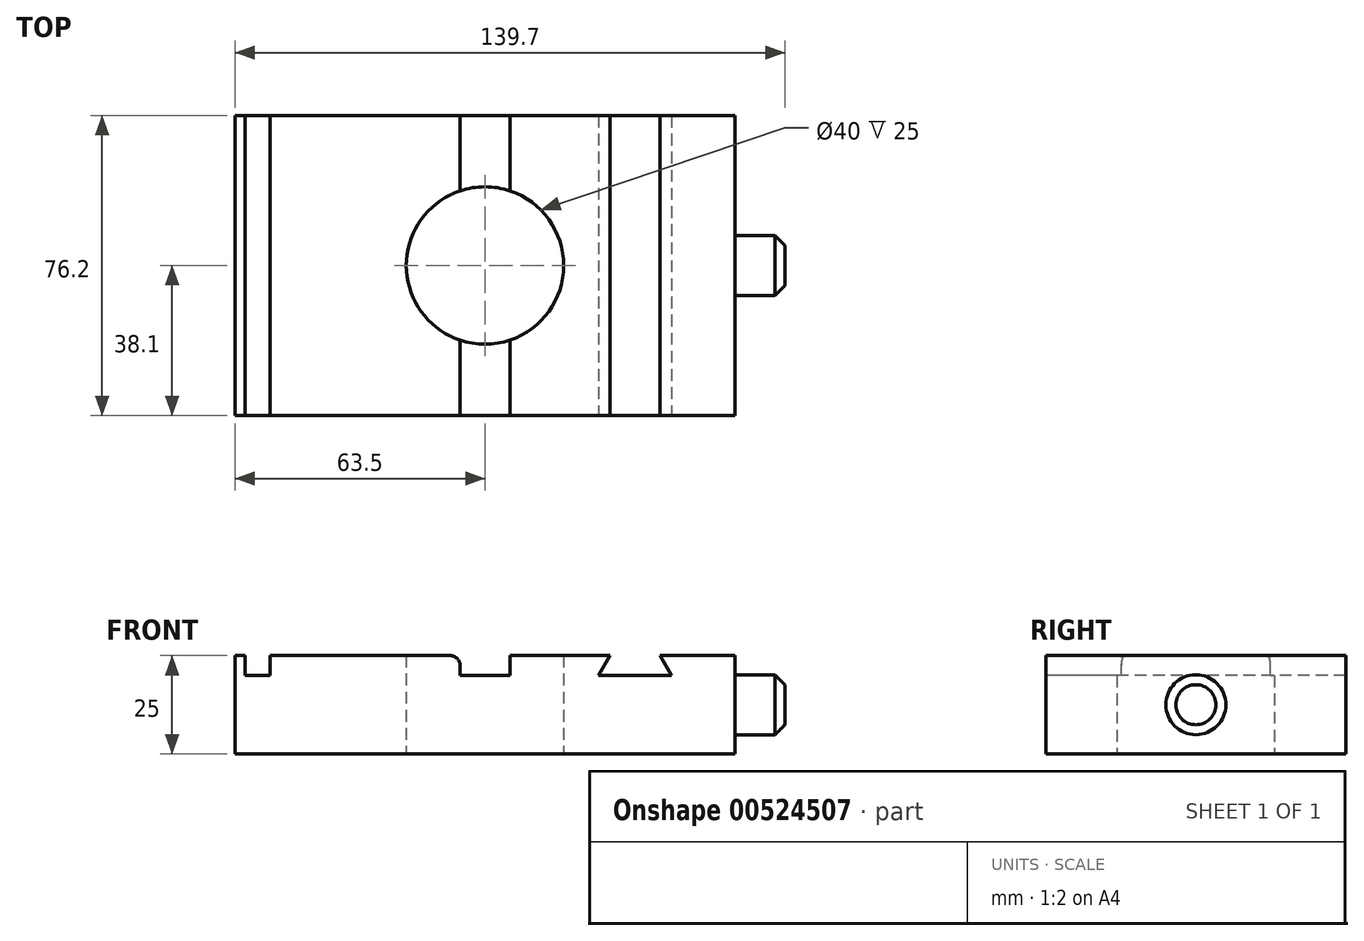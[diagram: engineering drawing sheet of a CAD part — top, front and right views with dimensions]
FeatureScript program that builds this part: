
annotation { "Feature Type Name" : "Feature", "Feature Type Description" : "" }
export const myFeature = defineFeature(function(context is Context, id is Id, definition is map)
    precondition{}
    {
        {
            var Q0;
            Q0=qCreatedBy(makeId("Top.planeOp"),FACE);
            var sketch = newSketch(context, id + "F0", { "sketchPlane" : qUnion([Q0])});
            skLineSegment(sketch, "E0.bottom", {"start": v(63.5, -38.1) * mm, "end": v(-63.5, -38.1) * mm});
            skLineSegment(sketch, "E0.top", {"start": v(63.5, 38.1) * mm, "end": v(-63.5, 38.1) * mm});
            skLineSegment(sketch, "E0.left", {"start": v(63.5, -38.1) * mm, "end": v(63.5, 38.1) * mm});
            skLineSegment(sketch, "E0.right", {"start": v(-63.5, -38.1) * mm, "end": v(-63.5, 38.1) * mm});
            skPoint(sketch, "E0.middle", {"position": v(0, 0) * mm});
            skCircle(sketch, "E1", {"center": v(0, 0) * mm, "radius": 20 * mm});
            skSolve(sketch);
        }
        {
            var Q0;
            Q0=makeQuery(id+"F0.imprint","IMPRINT",FACE,{"disambiguationData":[TD([[makeQuery(id+"F0.imprint","IMPRINT",EDGE,{"derivedFrom":sQuery(id+"F0.wireOp",EDGE,"E0.bottom")}),-1.0]])]});
            extrude(context, id + "F1", {"entities" : qUnion([Q0]), "depth" : 25 * mm, "offsetDistance" : 25 * mm});
        }
        {
            var Q0;
            Q0=makeQuery(id+"F1.opExtrude","CAP_FACE",FACE,{"disambiguationData":[OSD([sQuery(id+"F0.wireOp",EDGE,"E0.bottom"),sQuery(id+"F0.wireOp",EDGE,"E0.top"),sQuery(id+"F0.wireOp",EDGE,"E0.left"),sQuery(id+"F0.wireOp",EDGE,"E0.right"),sQuery(id+"F0.wireOp",EDGE,"E1")])],"isStart":false});
            var sketch = newSketch(context, id + "F2", { "sketchPlane" : qUnion([Q0])});
            skLineSegment(sketch, "E2.bottom", {"start": v(-60.96, 38.1) * mm, "end": v(-54.6, 38.1) * mm});
            skLineSegment(sketch, "E2.top", {"start": v(-60.96, -38.1) * mm, "end": v(-54.6, -38.1) * mm});
            skLineSegment(sketch, "E2.left", {"start": v(-60.96, 38.1) * mm, "end": v(-60.96, -38.1) * mm});
            skLineSegment(sketch, "E2.right", {"start": v(-54.6, 38.1) * mm, "end": v(-54.6, -38.1) * mm});
            skLineSegment(sketch, "E3", {"start": v(-6.35, 38.1) * mm, "end": v(-6.35, -38.1) * mm});
            skLineSegment(sketch, "E4", {"start": v(-6.35, -38.1) * mm, "end": v(6.35, -38.1) * mm});
            skLineSegment(sketch, "E5", {"start": v(6.35, -38.1) * mm, "end": v(6.35, 38.1) * mm});
            skPoint(sketch, "E6", {"position": v(0, 0) * mm});
            skLineSegment(sketch, "E7", {"start": v(-6.35, 38.1) * mm, "end": v(6.35, 38.1) * mm, "construction": true});
            skLineSegment(sketch, "E8", {"start": v(0, 38.1) * mm, "end": v(0, -38.1) * mm, "construction": true});
            skSolve(sketch);
        }
        {
            var Q0;
            Q0=makeQuery(id+"F2.imprint","IMPRINT",FACE,{"disambiguationData":[TD([[makeQuery(id+"F2.imprint","IMPRINT",EDGE,{"derivedFrom":sQuery(id+"F2.wireOp",EDGE,"E2.bottom")}),1.0]])]});
            var Q1;
            {var subQ0=sQuery(id+"F2.wireOp",EDGE,"E4");Q1=makeQuery(id+"F2.imprint","IMPRINT",FACE,{"disambiguationData":[TD([[makeQuery(id+"F2.imprint","IMPRINT",EDGE,{"derivedFrom":subQ0}),-1.0]])]});}
            var Q2;
            {var subQ0=sQuery(id+"F2.wireOp",EDGE,"E3");var subQ1=makeQuery(id+"F1.opExtrude","CAP_EDGE",EDGE,{"disambiguationData":[OSD([sQuery(id+"F0.wireOp",EDGE,"E0.top")])],"isStart":false});var subQ2=makeQuery(id+"F2.imprint","INTERSECT",VERTEX,{"derivedFrom":[subQ1,subQ0]});Q2=makeQuery(id+"F2.imprint","IMPRINT",FACE,{"disambiguationData":[TD([[makeQuery(id+"F2.imprint","IMPRINT",EDGE,{"disambiguationData":[TD([[subQ2,-1.0]])],"derivedFrom":subQ0}),1.0]])]});}
            extrude(context, id + "F3", {"entities" : qUnion([Q0, Q1, Q2]), "operationType" : NewBodyOperationType.REMOVE, "oppositeDirection" : true, "depth" : 5.08 * mm, "offsetDistance" : 25.4 * mm});
        }
        {
            var Q0;
            Q0=makeQuery(id+"F1.opExtrude","SWEPT_FACE",FACE,{"disambiguationData":[OSD([sQuery(id+"F0.wireOp",EDGE,"E0.bottom")])]});
            var sketch = newSketch(context, id + "F4", { "sketchPlane" : qUnion([Q0])});
            skLineSegment(sketch, "E9", {"start": v(31.75, 25) * mm, "end": v(28.82, 19.92) * mm});
            skLineSegment(sketch, "E10", {"start": v(28.82, 19.92) * mm, "end": v(47.38, 19.92) * mm});
            skLineSegment(sketch, "E11", {"start": v(47.38, 19.92) * mm, "end": v(44.45, 25) * mm});
            skLineSegment(sketch, "E12", {"start": v(44.45, 25) * mm, "end": v(31.75, 25) * mm});
            skLineSegment(sketch, "E13", {"start": v(38.1, 19.92) * mm, "end": v(38.1, 25) * mm, "construction": true});
            skSolve(sketch);
        }
        {
            var Q0;
            Q0=makeQuery(id+"F4.imprint","IMPRINT",FACE,{"disambiguationData":[TD([[makeQuery(id+"F4.imprint","IMPRINT",EDGE,{"derivedFrom":sQuery(id+"F4.wireOp",EDGE,"E9")}),1.0]])]});
            extrude(context, id + "F5", {"entities" : qUnion([Q0]), "operationType" : NewBodyOperationType.REMOVE, "endBound" : BoundingType.THROUGH_ALL, "oppositeDirection" : true, "depth" : 25.4 * mm, "offsetDistance" : 25.4 * mm});
        }
        {
            var Q0;
            Q0=makeQuery(id+"F1.opExtrude","SWEPT_FACE",FACE,{"disambiguationData":[OSD([sQuery(id+"F0.wireOp",EDGE,"E0.left")])]});
            var sketch = newSketch(context, id + "F6", { "sketchPlane" : qUnion([Q0])});
            skCircle(sketch, "E14", {"center": v(0, 12.5) * mm, "radius": 7.62 * mm});
            skPoint(sketch, "E14.centerSnap0", {"position": v(0, 25) * mm});
            skPoint(sketch, "E14.centerSnap1", {"position": v(-38.1, 12.5) * mm});
            skSolve(sketch);
        }
        {
            var Q0;
            Q0=makeQuery(id+"F6.imprint","IMPRINT",FACE,{"disambiguationData":[TD([[makeQuery(id+"F6.imprint","IMPRINT",EDGE,{"derivedFrom":sQuery(id+"F6.wireOp",EDGE,"E14")}),1.0]])]});
            extrude(context, id + "F7", {"entities" : qUnion([Q0]), "operationType" : NewBodyOperationType.ADD, "depth" : 12.7 * mm, "offsetDistance" : 25.4 * mm});
        }
        {
            var Q0;
            {var subQ0=sQuery(id+"F2.wireOp",EDGE,"E3");Q0=makeQuery(id+"F3.boolean.opBoolean","COPY",EDGE,{"derivedFrom":makeQuery(id+"F3.opExtrude","CAP_EDGE",EDGE,{"disambiguationData":[OSD([subQ0]),TDD([makeQuery(id+"F2.imprint","IMPRINT",EDGE,{"disambiguationData":[TD([[makeQuery(id+"F2.imprint","INTERSECT",VERTEX,{"disambiguationData":[OD(1.0)],"derivedFrom":[makeQuery(id+"F1.opExtrude","CAP_EDGE",EDGE,{"disambiguationData":[OSD([sQuery(id+"F0.wireOp",EDGE,"E1")])],"isStart":false}),subQ0]}),-1.0]])],"derivedFrom":subQ0})])],"isStart":true})});}
            var Q1;
            {var subQ0=sQuery(id+"F2.wireOp",EDGE,"E3");Q1=makeQuery(id+"F3.boolean.opBoolean","COPY",EDGE,{"derivedFrom":makeQuery(id+"F3.opExtrude","CAP_EDGE",EDGE,{"disambiguationData":[OSD([subQ0]),TDD([makeQuery(id+"F2.imprint","IMPRINT",EDGE,{"disambiguationData":[TD([[makeQuery(id+"F2.imprint","INTERSECT",VERTEX,{"derivedFrom":[makeQuery(id+"F1.opExtrude","CAP_EDGE",EDGE,{"disambiguationData":[OSD([sQuery(id+"F0.wireOp",EDGE,"E0.top")])],"isStart":false}),subQ0]}),-1.0]])],"derivedFrom":subQ0})])],"isStart":true})});}
            var Q2;
            {var subQ0=sQuery(id+"F2.wireOp",EDGE,"E5");Q2=makeQuery(id+"F3.boolean.opBoolean","COPY",EDGE,{"derivedFrom":makeQuery(id+"F3.opExtrude","CAP_EDGE",EDGE,{"disambiguationData":[OSD([subQ0]),TDD([makeQuery(id+"F2.imprint","IMPRINT",EDGE,{"disambiguationData":[TD([[makeQuery(id+"F2.imprint","INTERSECT",VERTEX,{"derivedFrom":[makeQuery(id+"F1.opExtrude","CAP_EDGE",EDGE,{"disambiguationData":[OSD([sQuery(id+"F0.wireOp",EDGE,"E0.top")])],"isStart":false}),subQ0]}),1.0]])],"derivedFrom":subQ0})])],"isStart":true})});}
            var Q3;
            {var subQ0=sQuery(id+"F2.wireOp",EDGE,"E5");Q3=makeQuery(id+"F3.boolean.opBoolean","COPY",EDGE,{"derivedFrom":makeQuery(id+"F3.opExtrude","CAP_EDGE",EDGE,{"disambiguationData":[OSD([subQ0]),TDD([makeQuery(id+"F2.imprint","IMPRINT",EDGE,{"disambiguationData":[TD([[makeQuery(id+"F2.imprint","INTERSECT",VERTEX,{"disambiguationData":[OD(0.0)],"derivedFrom":[makeQuery(id+"F1.opExtrude","CAP_EDGE",EDGE,{"disambiguationData":[OSD([sQuery(id+"F0.wireOp",EDGE,"E1")])],"isStart":false}),subQ0]}),1.0]])],"derivedFrom":subQ0})])],"isStart":true})});}
            fillet(context, id + "F8", {"entities" : qUnion([Q0, Q1, Q2, Q3]), "radius" : 2.54 * mm, "tangentPropagation" : true, "allowEdgeOverflow" : false});
        }
        {
            var Q0;
            Q0=makeQuery(id+"F7.opExtrude","CAP_FACE",FACE,{"disambiguationData":[OSD([sQuery(id+"F6.wireOp",EDGE,"E14")])],"isStart":false});
            chamfer(context, id + "F9", {"entities" : qUnion([Q0]), "width" : 2.54 * mm, "tangentPropagation" : true});
        }
    });
